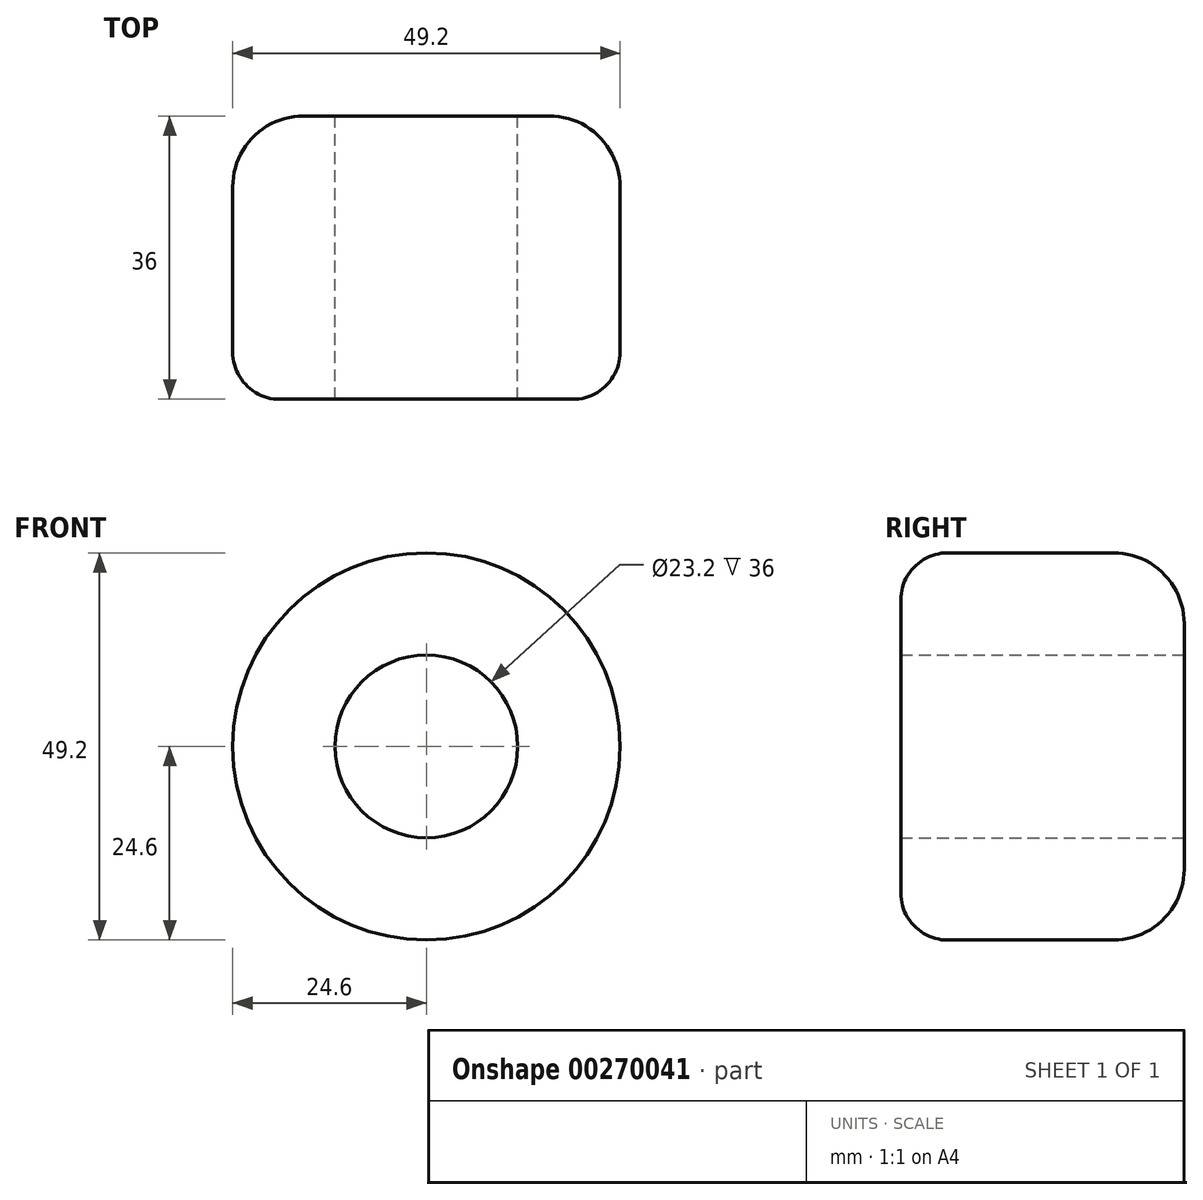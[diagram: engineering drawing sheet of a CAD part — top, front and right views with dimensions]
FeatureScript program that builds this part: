
annotation { "Feature Type Name" : "Feature", "Feature Type Description" : "" }
export const myFeature = defineFeature(function(context is Context, id is Id, definition is map)
    precondition{}
    {
        {
            var Q0;
            Q0=qCreatedBy(makeId("Front.planeOp"),FACE);
            var sketch = newSketch(context, id + "F0", { "sketchPlane" : qUnion([Q0])});
            skCircle(sketch, "E0", {"center": v(0, 0) * mm, "radius": 24.6 * mm});
            skCircle(sketch, "E1", {"center": v(0, 0) * mm, "radius": 11.6 * mm});
            skSolve(sketch);
        }
        {
            var Q0;
            Q0 = qSketchRegion(id + "F0", true);
            extrude(context, id + "F1", {"entities" : qUnion([Q0]), "depth" : 36 * mm});
        }
        {
            var Q0;
            Q0=makeQuery(id+"F1.opExtrude","CAP_EDGE",EDGE,{"disambiguationData":[OSD([sQuery(id+"F0.wireOp",EDGE,"E0")])],"isStart":true});
            fillet(context, id + "F2", {"entities" : qUnion([Q0]), "radius" : 9 * mm, "tangentPropagation" : true, "allowEdgeOverflow" : false});
        }
        {
            var Q0;
            Q0=makeQuery(id+"F1.opExtrude","CAP_EDGE",EDGE,{"disambiguationData":[OSD([sQuery(id+"F0.wireOp",EDGE,"E0")])],"isStart":false});
            fillet(context, id + "F3", {"entities" : qUnion([Q0]), "radius" : 6 * mm, "tangentPropagation" : true, "allowEdgeOverflow" : false});
        }
    });
